# Revit family: DLB060014
name_source: partatom
category: Appareils sanitaires
revit_build: Autodesk Revit 2015 (Build: 20140606_1530(x64)
units: mm (PartAtom-declared; Revit-internal decimal feet)

## types (1)
- Type 1
    Category = WC
    Commentaires du type = Wall-hung WC pan for people with reduced mobility
    Description = French manufacturer Delabie is a leader in the European sanitary ware market for non-domestic places. Water controls, solutions for disabled people, sanitary ware, for schools, leisure centres, offices, hospitals, airports…
    Fabricant = DELABIE
    Features  = Wall-hung WC pan.
700mm elongated pan for improved comfort for people with reduced mobility.
Compatible with all standard frame systems available on the market.
Elegant and simple design.
Bacteriostatic 304 stainless steel.
Stainless steel thickness: 1.5mm.
One-piece pressed WC bowl, seam-free for easy maintenance and better hygiene.
WC bowl surface is polished with rounded edges for easy cleaning.
Concealed perimetral flushing rim.
Horizontal water inlet: Ø 55mm.
Horizontal waste outlet: Ø 100mm.
Water saving: works with 4L or more of water.
Shrouded pan.
Pre-drilled holes for fixing the toilet seat. Supplied with stainless steel blanking caps when installed without toilet seat lid.
Quick and easy to install from the front thanks to a stainless steel mounting frame.
Supplied with fixing plate and 6 theft prevention TORX security screws.
CE marked. Complies with European standard EN 997 for 4L flush.
Optional toilet seat with or without lid.
Available for through-the-wall installation in service ducts.
Weight: 14.5kg.
    Finish = Polished satin
    Grade = CE
    ManufacturerName = DELABIE
    ManufacturerURL = http://www.delabie.com
    Material = 304 stainless steel
    ModelNumber = 110710
    Modèle = 700 S WC pan
    Name = 700 S WC pan
    NominalHeight = 350 mm  [stored 1.14829 ft]
    NominalLength = 360 mm  [stored 1.1811 ft]
    NominalWidth = 700 mm  [stored 2.29659 ft]
    ProductInformation = http://www.delabie.com
    Radius (In) = 55 mm  [stored 0.180446 ft]
    Radius (Out) = 100 mm  [stored 0.328084 ft]
    SerialNumber = 3456330153515
    URL = http://www.delabie.com
    Version = v1
    WarrantyDescription = Any manufacturing defect
    WarrantyDurationUnit = 10 years
    Weight = 14.5kg

note: [stored X ft] marks values corroborated as IEEE doubles in the binary element streams (Revit-internal decimal feet)

## geometry (parser evidence)
native form markers: Blend x24, Sweep x14
no freeform markers — native parametric forms only
